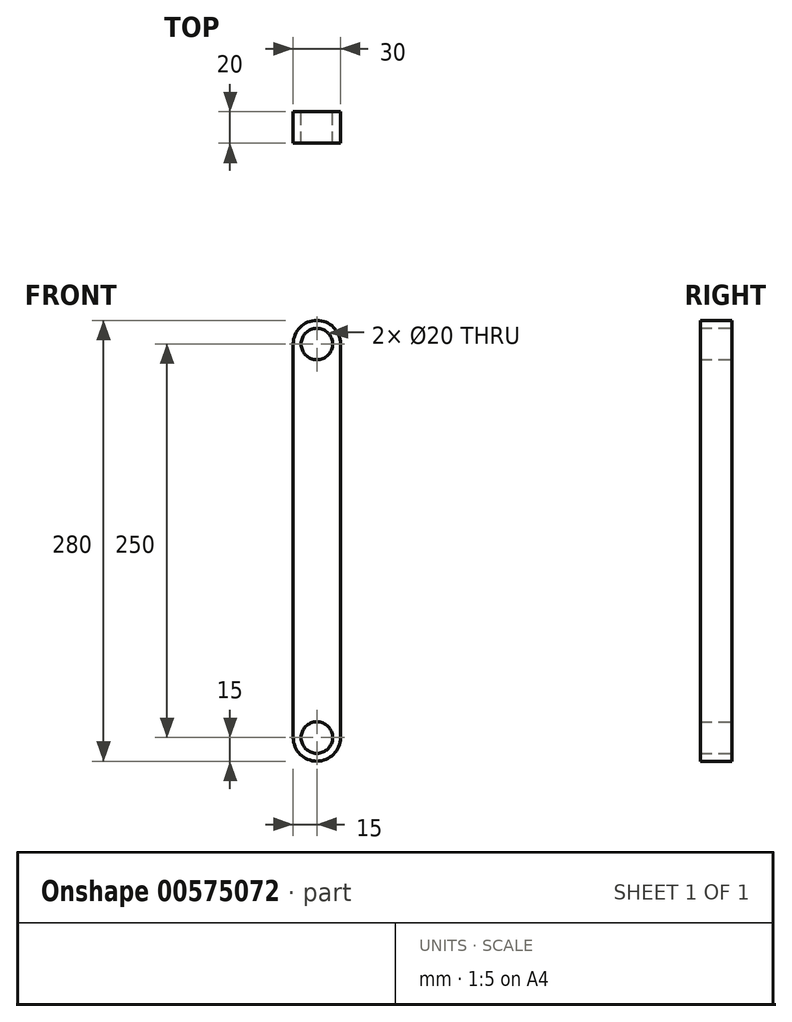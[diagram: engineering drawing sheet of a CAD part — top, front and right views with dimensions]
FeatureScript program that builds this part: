
annotation { "Feature Type Name" : "Feature", "Feature Type Description" : "" }
export const myFeature = defineFeature(function(context is Context, id is Id, definition is map)
    precondition{}
    {
        {
            var Q0;
            Q0=qCreatedBy(makeId("Front.planeOp"),FACE);
            var sketch = newSketch(context, id + "F0", { "sketchPlane" : qUnion([Q0])});
            skArc(sketch, "E0", {"start": v(15, 0) * mm, "mid": v(0, 15) * mm, "end": v(-15, 0) * mm});
            skLineSegment(sketch, "E1", {"start": v(-15, 0) * mm, "end": v(-15, -250) * mm});
            skLineSegment(sketch, "E2.MirrorCS", {"start": v(15, 0) * mm, "end": v(15, -250) * mm});
            skArc(sketch, "E3", {"start": v(-15, -250) * mm, "mid": v(0, -265) * mm, "end": v(15, -250) * mm});
            skCircle(sketch, "E4", {"center": v(0, 0) * mm, "radius": 10 * mm});
            skCircle(sketch, "E5", {"center": v(0, -250) * mm, "radius": 10 * mm});
            skSolve(sketch);
        }
        {
            var Q0;
            Q0=makeQuery(id+"F0.imprint","IMPRINT",FACE,{"disambiguationData":[TD([[makeQuery(id+"F0.imprint","IMPRINT",EDGE,{"derivedFrom":sQuery(id+"F0.wireOp",EDGE,"E0")}),1.0]])]});
            extrude(context, id + "F1", {"entities" : qUnion([Q0]), "depth" : 20 * mm, "offsetDistance" : 25 * mm, "symmetric" : true});
        }
    });
